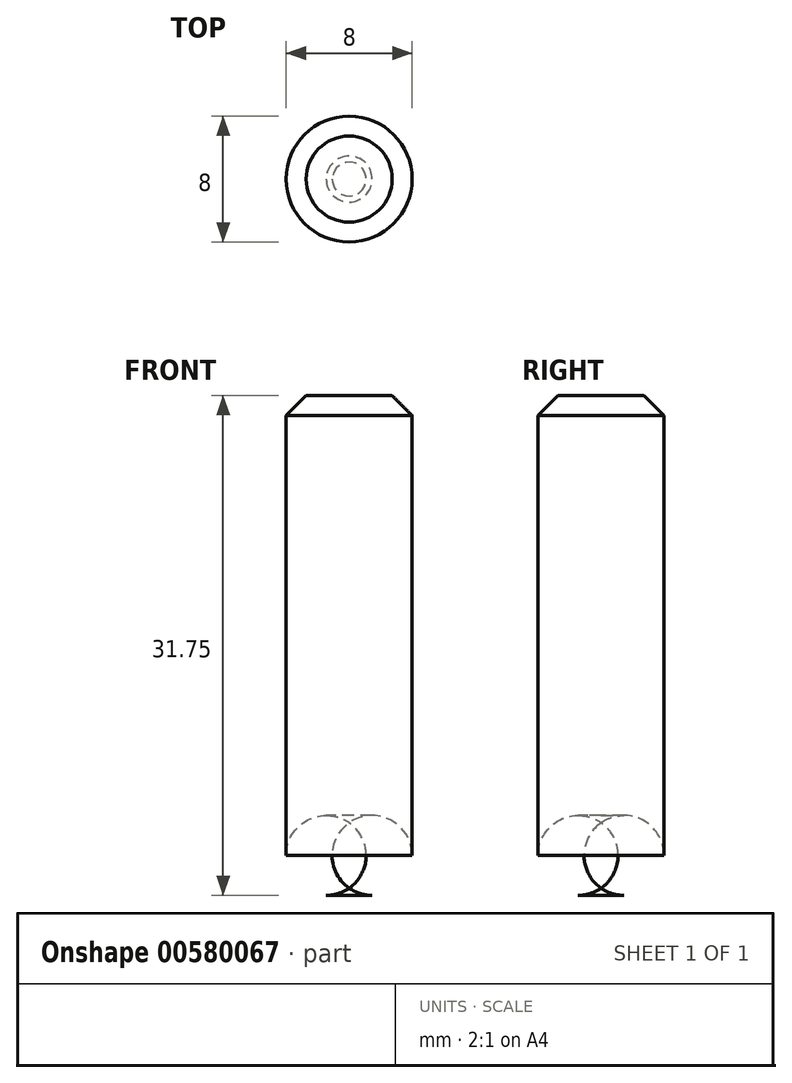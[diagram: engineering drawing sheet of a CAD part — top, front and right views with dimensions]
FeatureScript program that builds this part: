
annotation { "Feature Type Name" : "Feature", "Feature Type Description" : "" }
export const myFeature = defineFeature(function(context is Context, id is Id, definition is map)
    precondition{}
    {
        {
            var Q0;
            Q0=qCreatedBy(makeId("Top.planeOp"),FACE);
            var sketch = newSketch(context, id + "F0", { "sketchPlane" : qUnion([Q0])});
            skCircle(sketch, "E0", {"center": v(0, 0) * mm, "radius": 4 * mm});
            skSolve(sketch);
        }
        {
            var Q0;
            Q0 = qSketchRegion(id + "F0", true);
            extrude(context, id + "F1", {"entities" : qUnion([Q0]), "depth" : 31.75 * mm, "offsetDistance" : 25.4 * mm});
        }
        {
            var Q0;
            Q0=makeQuery(id+"F1.opExtrude","CAP_EDGE",EDGE,{"disambiguationData":[OSD([sQuery(id+"F0.wireOp",EDGE,"E0")])],"isStart":false});
            chamfer(context, id + "F2", {"entities" : qUnion([Q0]), "width" : 1.27 * mm, "tangentPropagation" : true});
        }
        {
            var Q0;
            Q0=makeQuery(id+"F1.opExtrude","CAP_EDGE",EDGE,{"disambiguationData":[OSD([sQuery(id+"F0.wireOp",EDGE,"E0")])],"isStart":true});
            fillet(context, id + "F3", {"entities" : qUnion([Q0]), "radius" : 2.54 * mm, "tangentPropagation" : true, "allowEdgeOverflow" : false});
        }
    });
